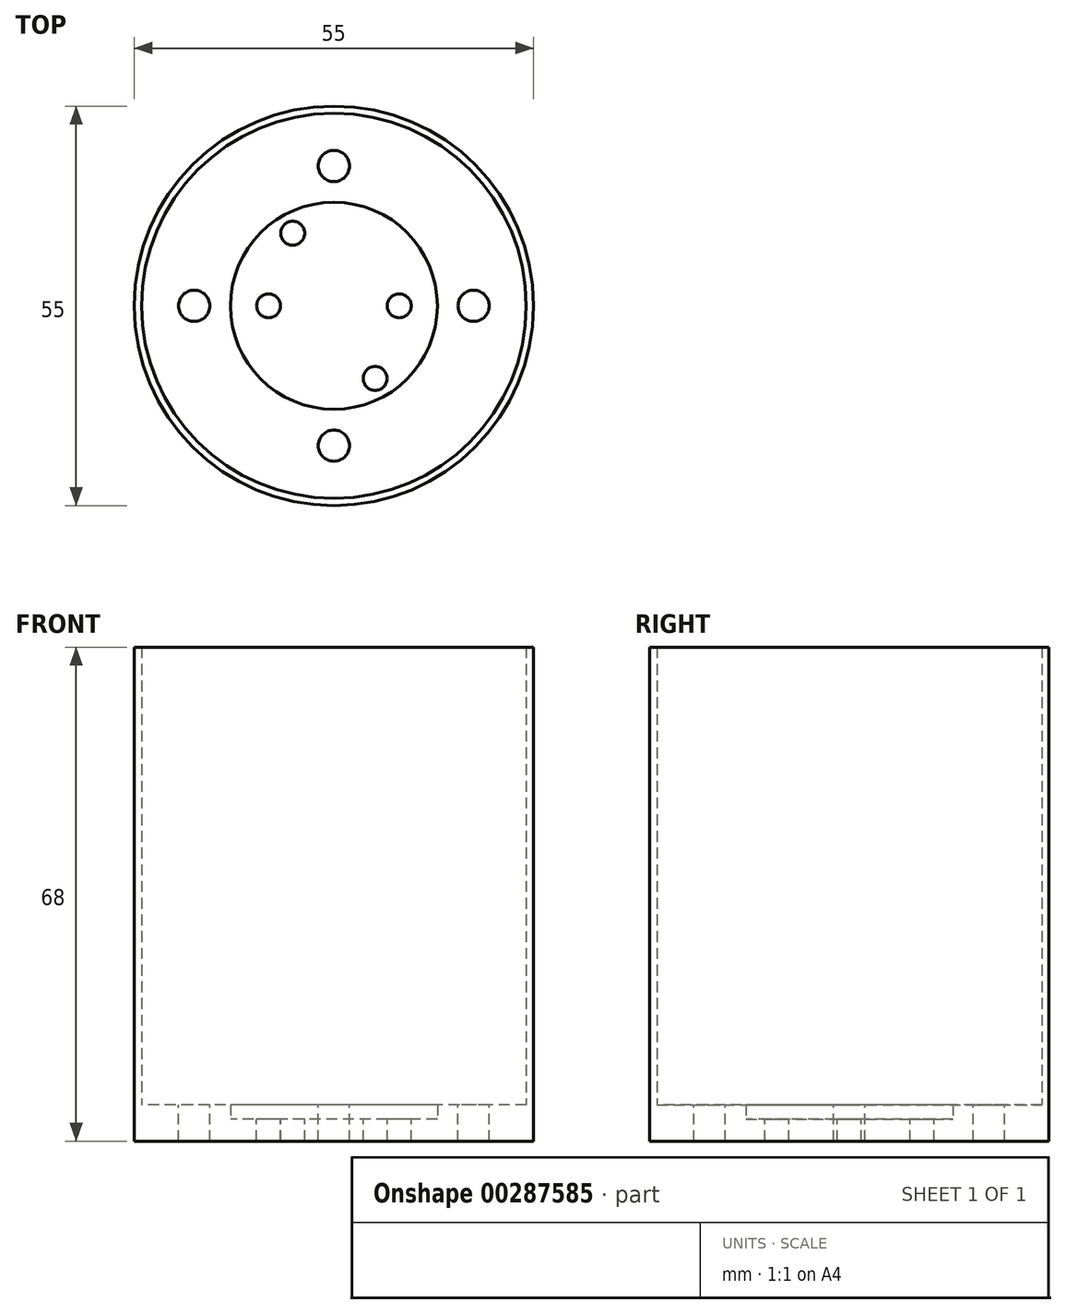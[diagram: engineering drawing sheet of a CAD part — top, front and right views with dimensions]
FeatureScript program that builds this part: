
annotation { "Feature Type Name" : "Feature", "Feature Type Description" : "" }
export const myFeature = defineFeature(function(context is Context, id is Id, definition is map)
    precondition{}
    {
        {
            var Q0;
            Q0=qCreatedBy(makeId("Top.planeOp"),FACE);
            var sketch = newSketch(context, id + "F0", { "sketchPlane" : qUnion([Q0])});
            skCircle(sketch, "E0", {"center": v(0, 0) * mm, "radius": 26.5 * mm});
            skCircle(sketch, "E1", {"center": v(0, 0) * mm, "radius": 27.5 * mm});
            skCircle(sketch, "E2", {"center": v(0, 0) * mm, "radius": 14.25 * mm});
            skLineSegment(sketch, "E3", {"start": v(-14.25, 0) * mm, "end": v(14.25, 0) * mm, "construction": true});
            skCircle(sketch, "E4", {"center": v(-9, 0) * mm, "radius": 1.65 * mm});
            skCircle(sketch, "E5.MirrorC", {"center": v(9, 0) * mm, "radius": 1.65 * mm});
            skCircle(sketch, "E6", {"center": v(-5.68, 10) * mm, "radius": 1.65 * mm});
            skCircle(sketch, "E7", {"center": v(0, 0) * mm, "radius": 11.5 * mm, "construction": true});
            skLineSegment(sketch, "E8", {"start": v(-5.68, 10) * mm, "end": v(5.68, -10) * mm, "construction": true});
            skCircle(sketch, "E9", {"center": v(5.68, -10) * mm, "radius": 1.65 * mm});
            skCircle(sketch, "E10", {"center": v(0, 0) * mm, "radius": 19.25 * mm, "construction": true});
            skCircle(sketch, "E11", {"center": v(-19.25, 0) * mm, "radius": 2.15 * mm});
            skCircle(sketch, "E12.MirrorC", {"center": v(19.25, 0) * mm, "radius": 2.15 * mm});
            skCircle(sketch, "E13", {"center": v(0, -19.25) * mm, "radius": 2.15 * mm});
            skCircle(sketch, "E14.MirrorC", {"center": v(0, 19.25) * mm, "radius": 2.15 * mm});
            skSolve(sketch);
        }
        {
            var Q0;
            Q0=makeQuery(id+"F0.imprint","IMPRINT",FACE,{"disambiguationData":[TD([[makeQuery(id+"F0.imprint","IMPRINT",EDGE,{"derivedFrom":sQuery(id+"F0.wireOp",EDGE,"E0")}),-1.0]])]});
            extrude(context, id + "F1", {"entities" : qUnion([Q0]), "depth" : 65 * mm, "offsetDistance" : 25 * mm});
        }
        {
            var Q0;
            Q0=makeQuery(id+"F0.imprint","IMPRINT",FACE,{"disambiguationData":[TD([[makeQuery(id+"F0.imprint","IMPRINT",EDGE,{"derivedFrom":sQuery(id+"F0.wireOp",EDGE,"E0")}),-1.0]])]});
            var Q1;
            Q1=makeQuery(id+"F0.imprint","IMPRINT",FACE,{"disambiguationData":[TD([[makeQuery(id+"F0.imprint","IMPRINT",EDGE,{"derivedFrom":sQuery(id+"F0.wireOp",EDGE,"E0")}),1.0]])]});
            var Q2;
            Q2=makeQuery(id+"F0.imprint","IMPRINT",FACE,{"disambiguationData":[TD([[makeQuery(id+"F0.imprint","IMPRINT",EDGE,{"derivedFrom":sQuery(id+"F0.wireOp",EDGE,"E2")}),1.0]])]});
            extrude(context, id + "F2", {"entities" : qUnion([Q0, Q1, Q2]), "operationType" : NewBodyOperationType.ADD, "oppositeDirection" : true, "depth" : 3 * mm, "offsetDistance" : 25 * mm});
        }
        {
            var Q0;
            Q0=makeQuery(id+"F0.imprint","IMPRINT",FACE,{"disambiguationData":[TD([[makeQuery(id+"F0.imprint","IMPRINT",EDGE,{"derivedFrom":sQuery(id+"F0.wireOp",EDGE,"E0")}),1.0]])]});
            extrude(context, id + "F3", {"entities" : qUnion([Q0]), "operationType" : NewBodyOperationType.ADD, "depth" : 2 * mm, "offsetDistance" : 25 * mm});
        }
    });
